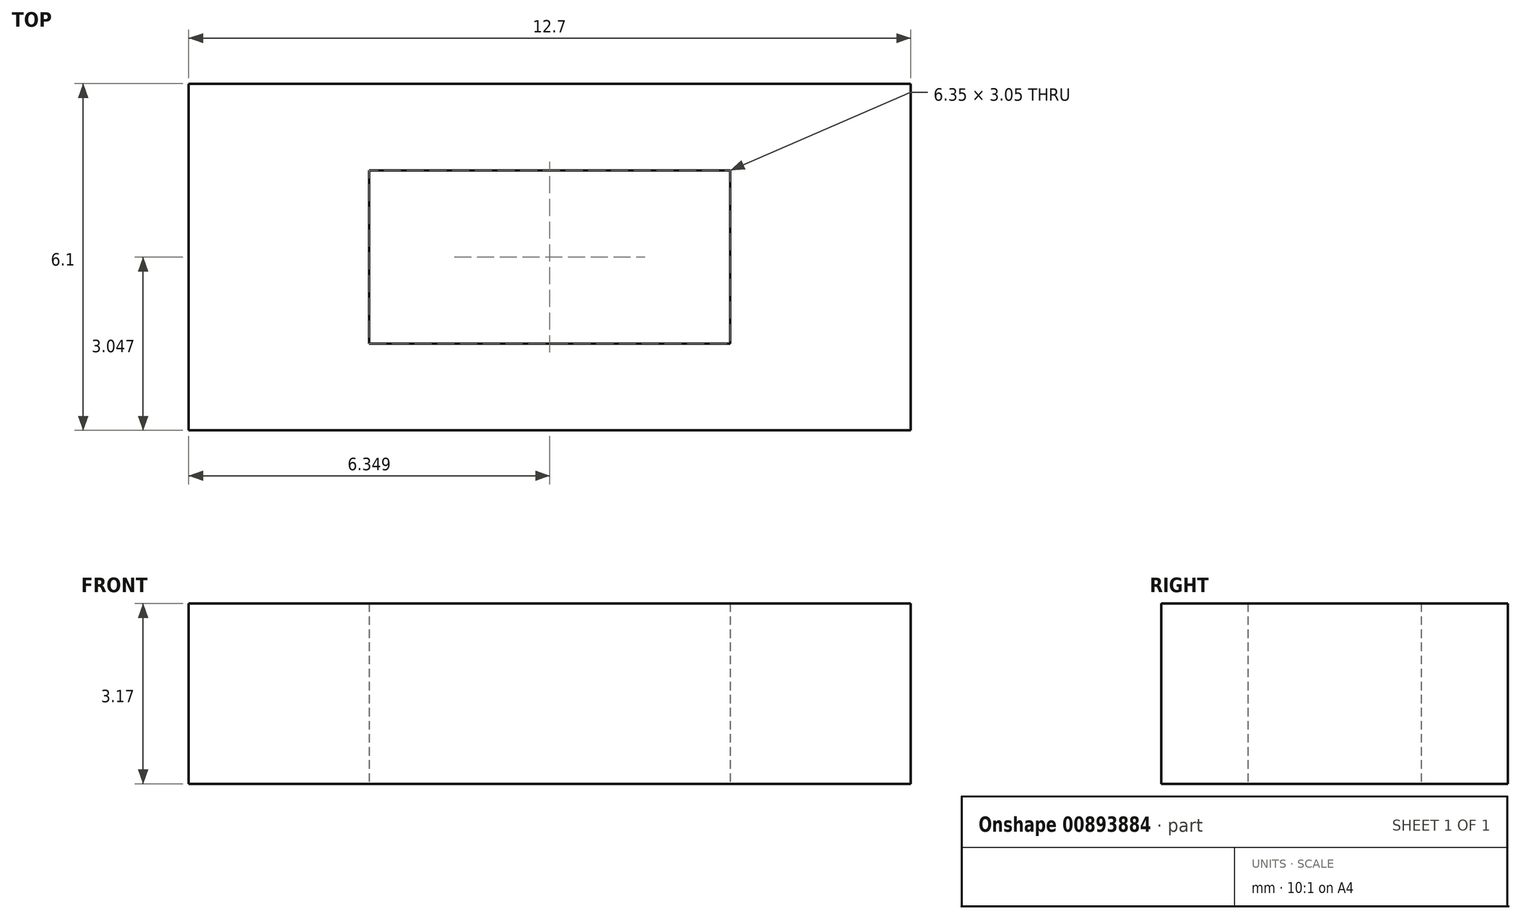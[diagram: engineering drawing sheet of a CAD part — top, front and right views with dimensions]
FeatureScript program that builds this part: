
annotation { "Feature Type Name" : "Feature", "Feature Type Description" : "" }
export const myFeature = defineFeature(function(context is Context, id is Id, definition is map)
    precondition{}
    {
        {
            var Q0;
            Q0=qCreatedBy(makeId("Top.planeOp"),FACE);
            var sketch = newSketch(context, id + "F0", { "sketchPlane" : qUnion([Q0])});
            skLineSegment(sketch, "E0.bottom", {"start": v(-3.6, -0.37) * mm, "end": v(9.1, -0.37) * mm});
            skLineSegment(sketch, "E0.top", {"start": v(-3.6, -6.47) * mm, "end": v(9.1, -6.47) * mm});
            skLineSegment(sketch, "E0.left", {"start": v(-3.6, -0.37) * mm, "end": v(-3.6, -6.47) * mm});
            skLineSegment(sketch, "E0.right", {"start": v(9.1, -0.37) * mm, "end": v(9.1, -6.47) * mm});
            skLineSegment(sketch, "E1.bottom", {"start": v(-0.43, -1.9) * mm, "end": v(5.92, -1.9) * mm});
            skLineSegment(sketch, "E1.top", {"start": v(-0.43, -4.95) * mm, "end": v(5.92, -4.95) * mm});
            skLineSegment(sketch, "E1.left", {"start": v(-0.43, -1.9) * mm, "end": v(-0.43, -4.95) * mm});
            skLineSegment(sketch, "E1.right", {"start": v(5.92, -1.9) * mm, "end": v(5.92, -4.95) * mm});
            skSolve(sketch);
        }
        {
            var Q0;
            Q0 = qSketchRegion(id + "F0", true);
            extrude(context, id + "F1", {"entities" : qUnion([Q0]), "depth" : 3.17 * mm, "offsetDistance" : 25.4 * mm});
        }
    });
